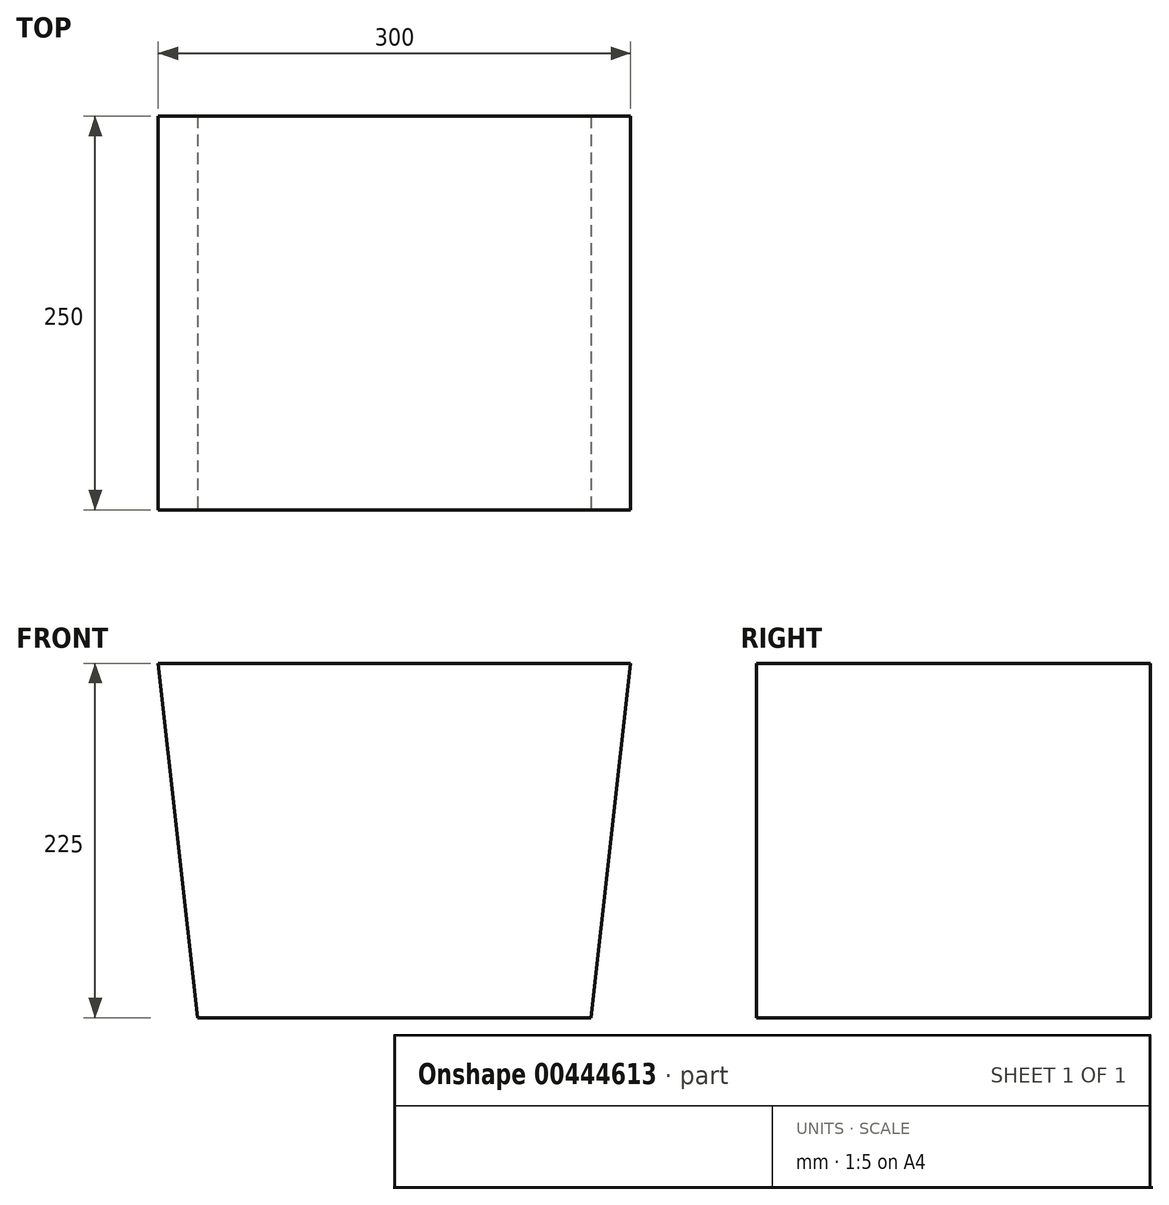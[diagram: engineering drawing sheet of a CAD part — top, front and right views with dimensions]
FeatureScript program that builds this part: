
annotation { "Feature Type Name" : "Feature", "Feature Type Description" : "" }
export const myFeature = defineFeature(function(context is Context, id is Id, definition is map)
    precondition{}
    {
        {
            var Q0;
            Q0=qCreatedBy(makeId("Front.planeOp"),FACE);
            var sketch = newSketch(context, id + "F0", { "sketchPlane" : qUnion([Q0])});
            skLineSegment(sketch, "E0.bottom", {"start": v(125, -112.5) * mm, "end": v(-125, -112.5) * mm});
            skPoint(sketch, "E0.middle", {"position": v(0, 0) * mm});
            skLineSegment(sketch, "E1", {"start": v(-150, 112.5) * mm, "end": v(-125, -112.5) * mm});
            skLineSegment(sketch, "E2", {"start": v(125, -112.5) * mm, "end": v(150, 112.5) * mm});
            skLineSegment(sketch, "E3", {"start": v(-150, 112.5) * mm, "end": v(150, 112.5) * mm});
            skSolve(sketch);
        }
        {
            var Q0;
            Q0=makeQuery(id+"F0.imprint","IMPRINT",FACE,{"disambiguationData":[TD([[makeQuery(id+"F0.imprint","IMPRINT",EDGE,{"derivedFrom":sQuery(id+"F0.wireOp",EDGE,"E0.bottom")}),-1.0]])]});
            extrude(context, id + "F1", {"entities" : qUnion([Q0]), "oppositeDirection" : true, "depth" : 250 * mm});
        }
    });
